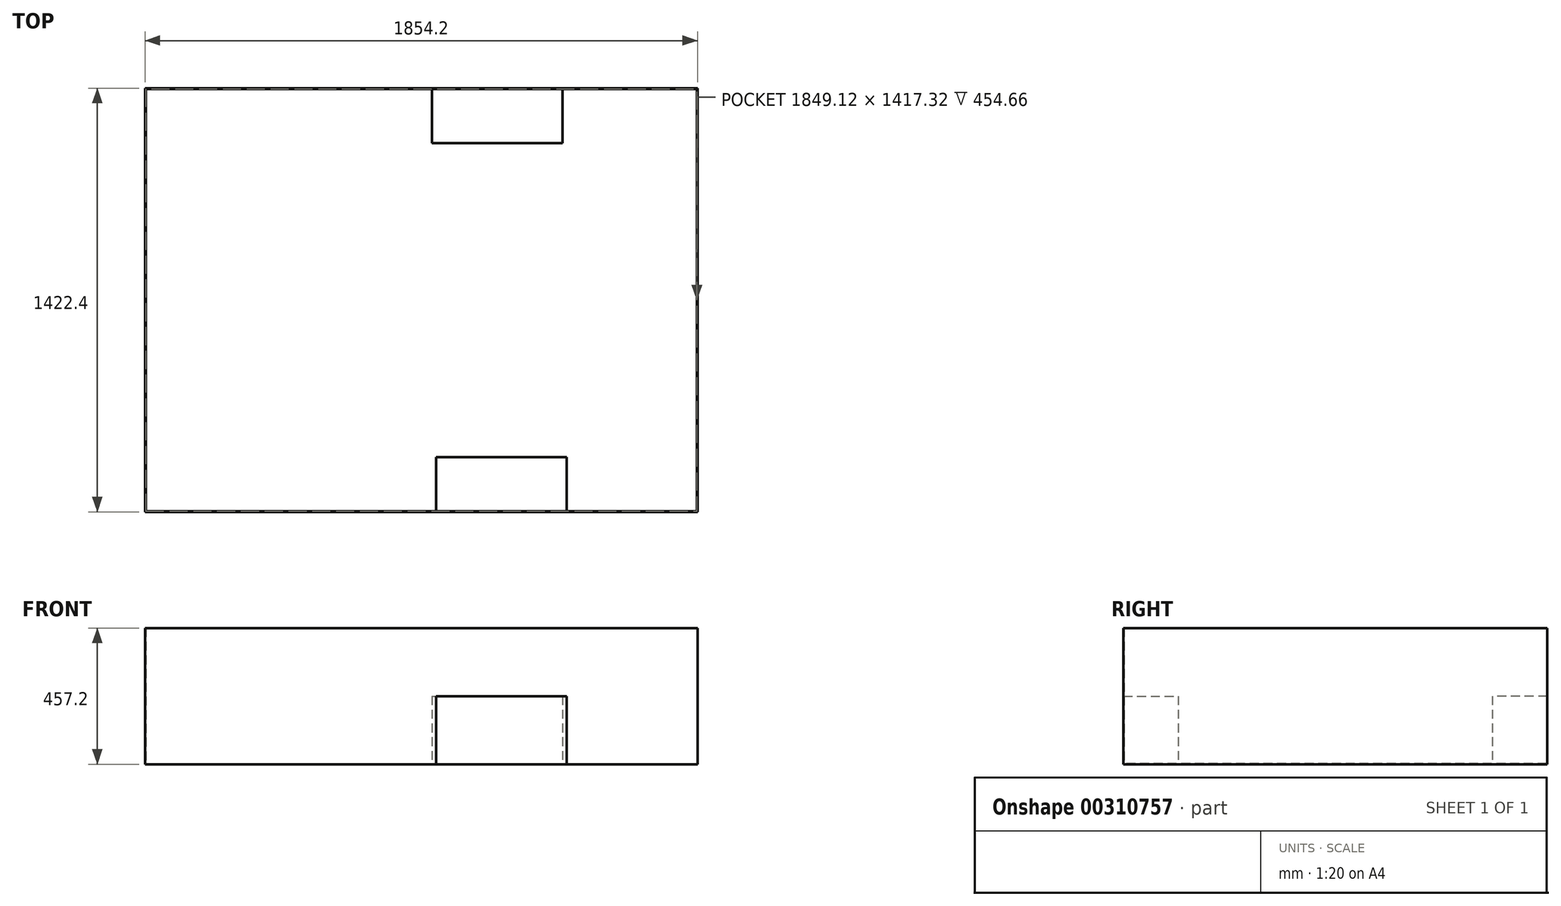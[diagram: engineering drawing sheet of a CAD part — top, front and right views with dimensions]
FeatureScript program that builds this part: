
annotation { "Feature Type Name" : "Feature", "Feature Type Description" : "" }
export const myFeature = defineFeature(function(context is Context, id is Id, definition is map)
    precondition{}
    {
        {
            var Q0;
            Q0=qCreatedBy(makeId("Top.planeOp"),FACE);
            var sketch = newSketch(context, id + "F0", { "sketchPlane" : qUnion([Q0])});
            skLineSegment(sketch, "E0.bottom", {"start": v(-245.88, 1271.22) * mm, "end": v(1608.32, 1271.22) * mm});
            skLineSegment(sketch, "E0.top", {"start": v(-245.88, -151.18) * mm, "end": v(1608.32, -151.18) * mm});
            skLineSegment(sketch, "E0.left", {"start": v(-245.88, 1271.22) * mm, "end": v(-245.88, -151.18) * mm});
            skLineSegment(sketch, "E0.right", {"start": v(1608.32, 1271.22) * mm, "end": v(1608.32, -151.18) * mm});
            skLineSegment(sketch, "E1.bottom", {"start": v(1155.58, 1271.22) * mm, "end": v(716.7, 1271.22) * mm});
            skLineSegment(sketch, "E1.top", {"start": v(1155.58, 1087.07) * mm, "end": v(716.7, 1087.07) * mm});
            skLineSegment(sketch, "E1.left", {"start": v(1155.58, 1271.22) * mm, "end": v(1155.58, 1087.07) * mm});
            skLineSegment(sketch, "E1.right", {"start": v(716.7, 1271.22) * mm, "end": v(716.7, 1087.07) * mm});
            skLineSegment(sketch, "E2.bottom", {"start": v(1169.53, -151.18) * mm, "end": v(730.65, -151.18) * mm});
            skLineSegment(sketch, "E2.top", {"start": v(1169.53, 32.97) * mm, "end": v(730.65, 32.97) * mm});
            skLineSegment(sketch, "E2.left", {"start": v(1169.53, -151.18) * mm, "end": v(1169.53, 32.97) * mm});
            skLineSegment(sketch, "E2.right", {"start": v(730.65, -151.18) * mm, "end": v(730.65, 32.97) * mm});
            skSolve(sketch);
        }
        {
            var Q0;
            Q0=makeQuery(id+"F0.imprint","IMPRINT",FACE,{"disambiguationData":[TD([[makeQuery(id+"F0.imprint","IMPRINT",EDGE,{"derivedFrom":sQuery(id+"F0.wireOp",EDGE,"E2.top")}),1.0]])]});
            var Q1;
            Q1=makeQuery(id+"F0.imprint","IMPRINT",FACE,{"disambiguationData":[TD([[makeQuery(id+"F0.imprint","IMPRINT",EDGE,{"derivedFrom":sQuery(id+"F0.wireOp",EDGE,"E1.top")}),-1.0]])]});
            extrude(context, id + "F1", {"entities" : qUnion([Q0, Q1]), "depth" : 228.6 * mm, "offsetDistance" : 25.4 * mm});
        }
        {
            var Q0;
            Q0 = qSketchRegion(id + "F0", true);
            extrude(context, id + "F2", {"entities" : qUnion([Q0]), "depth" : 457.2 * mm, "offsetDistance" : 25.4 * mm});
        }
        {
            var Q0;
            Q0=makeQuery(id+"F2.opExtrude","CAP_FACE",FACE,{"disambiguationData":[OSD([sQuery(id+"F0.wireOp",EDGE,"E0.bottom"),sQuery(id+"F0.wireOp",EDGE,"E0.top"),sQuery(id+"F0.wireOp",EDGE,"E0.left"),sQuery(id+"F0.wireOp",EDGE,"E0.right")])],"isStart":false});
            shell(context, id + "F3", {"entities" : qUnion([Q0]), "thickness" : 2.54 * mm});
        }
    });
